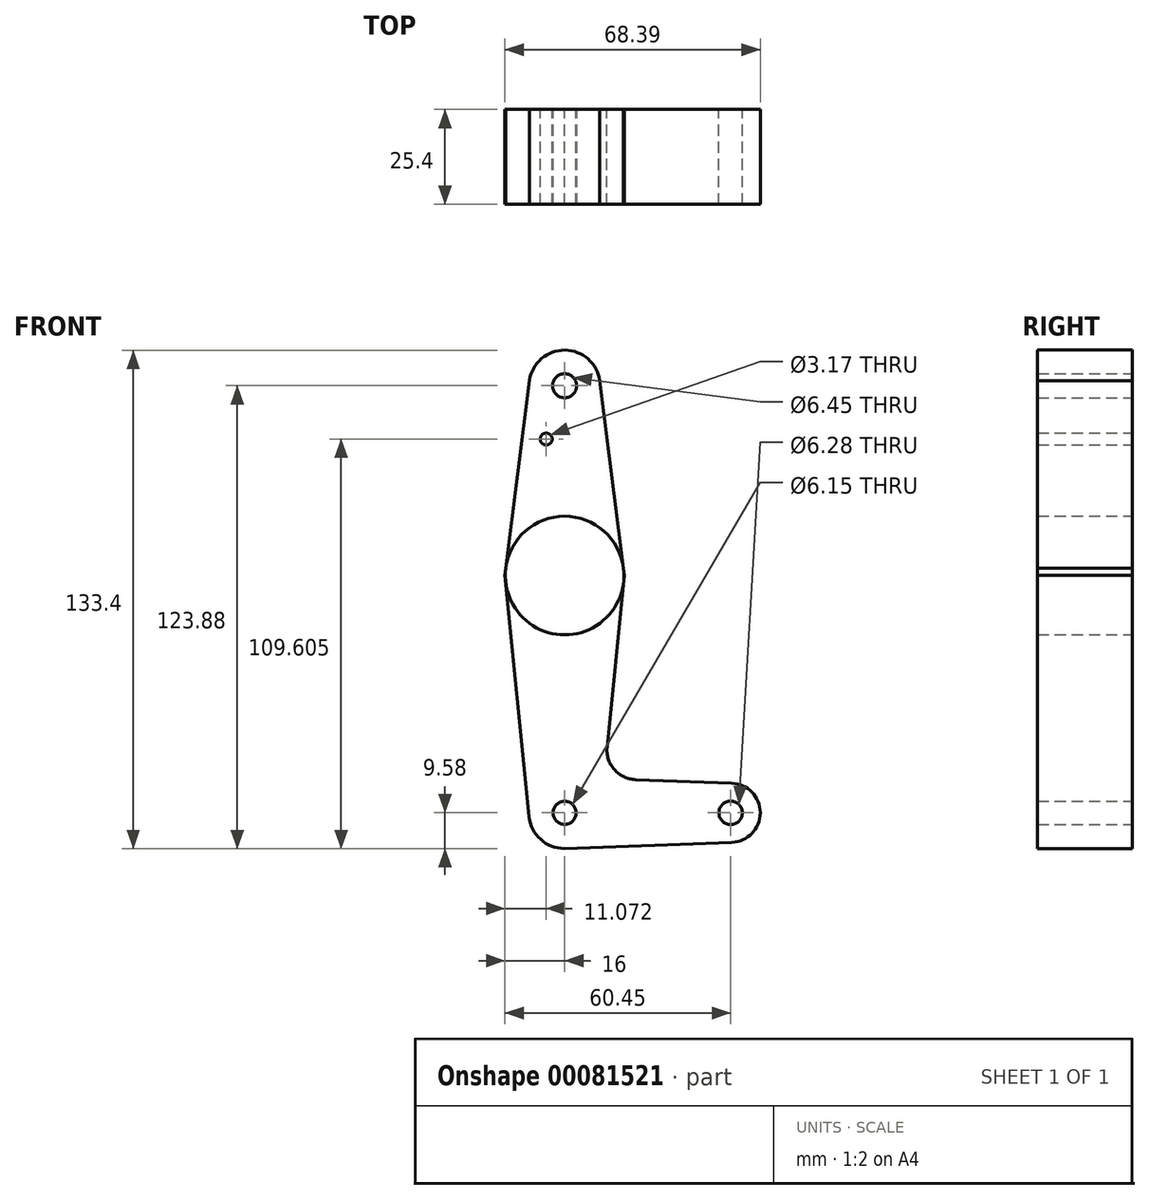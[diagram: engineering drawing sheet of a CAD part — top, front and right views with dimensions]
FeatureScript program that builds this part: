
annotation { "Feature Type Name" : "Feature", "Feature Type Description" : "" }
export const myFeature = defineFeature(function(context is Context, id is Id, definition is map)
    precondition{}
    {
        {
            var Q0;
            Q0=qCreatedBy(makeId("Front.planeOp"),FACE);
            var sketch = newSketch(context, id + "F0", { "sketchPlane" : qUnion([Q0])});
            skLineSegment(sketch, "E0", {"start": v(0, 50.8) * mm, "end": v(0, -63.5) * mm});
            skLineSegment(sketch, "E1", {"start": v(44.45, -63.5) * mm, "end": v(0, -63.5) * mm});
            skCircle(sketch, "E2", {"center": v(0, 50.8) * mm, "radius": 9.53 * mm});
            skCircle(sketch, "E3", {"center": v(0, 0) * mm, "radius": 15.88 * mm});
            skCircle(sketch, "E4", {"center": v(44.45, -63.5) * mm, "radius": 7.94 * mm});
            skCircle(sketch, "E5", {"center": v(0, -63.5) * mm, "radius": 9.58 * mm});
            skLineSegment(sketch, "E6", {"start": v(-9.42, 52.24) * mm, "end": v(-16, 0) * mm});
            skLineSegment(sketch, "E7", {"start": v(-16, 0) * mm, "end": v(-9.53, -64.46) * mm});
            skLineSegment(sketch, "E8", {"start": v(9.44, 52.09) * mm, "end": v(16, 0) * mm});
            skLineSegment(sketch, "E9", {"start": v(16, 0) * mm, "end": v(11.36, -45.88) * mm});
            skLineSegment(sketch, "E10", {"start": v(18.98, -54.62) * mm, "end": v(44.74, -55.57) * mm});
            skLineSegment(sketch, "E11", {"start": v(0, -73.08) * mm, "end": v(44.74, -71.43) * mm});
            skCircle(sketch, "E12", {"center": v(0, -63.5) * mm, "radius": 3.07 * mm});
            skCircle(sketch, "E13", {"center": v(44.45, -63.5) * mm, "radius": 3.14 * mm});
            skCircle(sketch, "E14", {"center": v(0, 0) * mm, "radius": 3.58 * mm});
            skCircle(sketch, "E15", {"center": v(0, 50.8) * mm, "radius": 3.23 * mm});
            skCircle(sketch, "E16", {"center": v(-4.93, 36.53) * mm, "radius": 1.59 * mm});
            skArc(sketch, "E17.filletArc", {"start": v(11.36, -45.88) * mm, "mid": v(13.27, -51.9) * mm, "end": v(18.98, -54.62) * mm});
            skSolve(sketch);
        }
        {
            var Q0;
            {var subQ0=sQuery(id+"F0.wireOp",EDGE,"E2");var subQ1=sQuery(id+"F0.wireOp",EDGE,"E0");var subQ2=makeQuery(id+"F0.imprint","INTERSECT",VERTEX,{"derivedFrom":[subQ1,subQ0]});Q0=makeQuery(id+"F0.imprint","IMPRINT",FACE,{"disambiguationData":[TD([[makeQuery(id+"F0.imprint","IMPRINT",EDGE,{"disambiguationData":[TD([[subQ2,-1.0]])],"derivedFrom":subQ1}),1.0]])]});}
            var Q1;
            Q1=makeQuery(id+"F0.imprint","IMPRINT",FACE,{"disambiguationData":[TD([[makeQuery(id+"F0.imprint","IMPRINT",EDGE,{"derivedFrom":sQuery(id+"F0.wireOp",EDGE,"E16")}),-1.0]])]});
            var Q2;
            {var subQ0=sQuery(id+"F0.wireOp",EDGE,"E3");var subQ2=sQuery(id+"F0.wireOp",EDGE,"E0");var subQ3=makeQuery(id+"F0.imprint","INTERSECT",VERTEX,{"disambiguationData":[OD(0.0)],"derivedFrom":[subQ2,subQ0]});Q2=makeQuery(id+"F0.imprint","IMPRINT",FACE,{"disambiguationData":[TD([[makeQuery(id+"F0.imprint","IMPRINT",EDGE,{"disambiguationData":[TD([[subQ3,-1.0]])],"derivedFrom":subQ2}),1.0]])]});}
            var Q3;
            {var subQ0=sQuery(id+"F0.wireOp",EDGE,"E3");var subQ2=sQuery(id+"F0.wireOp",EDGE,"E0");var subQ4=makeQuery(id+"F0.imprint","INTERSECT",VERTEX,{"disambiguationData":[OD(0.0)],"derivedFrom":[subQ2,subQ0]});Q3=makeQuery(id+"F0.imprint","IMPRINT",FACE,{"disambiguationData":[TD([[makeQuery(id+"F0.imprint","IMPRINT",EDGE,{"disambiguationData":[TD([[subQ4,-1.0]])],"derivedFrom":subQ2}),-1.0]])]});}
            var Q4;
            {var subQ0=sQuery(id+"F0.wireOp",EDGE,"E7");Q4=makeQuery(id+"F0.imprint","IMPRINT",FACE,{"disambiguationData":[TD([[makeQuery(id+"F0.imprint","IMPRINT",EDGE,{"derivedFrom":subQ0}),1.0]])]});}
            var Q5;
            {var subQ12=sQuery(id+"F0.wireOp",EDGE,"E9");Q5=makeQuery(id+"F0.imprint","IMPRINT",FACE,{"disambiguationData":[TD([[makeQuery(id+"F0.imprint","IMPRINT",EDGE,{"derivedFrom":subQ12}),-1.0]])]});}
            var Q6;
            {var subQ0=sQuery(id+"F0.wireOp",EDGE,"E4");var subQ1=sQuery(id+"F0.wireOp",EDGE,"E1");var subQ2=makeQuery(id+"F0.imprint","INTERSECT",VERTEX,{"derivedFrom":[subQ1,subQ0]});Q6=makeQuery(id+"F0.imprint","IMPRINT",FACE,{"disambiguationData":[TD([[makeQuery(id+"F0.imprint","IMPRINT",EDGE,{"disambiguationData":[TD([[subQ2,-1.0]])],"derivedFrom":subQ1}),1.0]])]});}
            var Q7;
            Q7=makeQuery(id+"F0.imprint","IMPRINT",FACE,{"disambiguationData":[TD([[makeQuery(id+"F0.imprint","IMPRINT",EDGE,{"derivedFrom":sQuery(id+"F0.wireOp",EDGE,"E15")}),-1.0]])]});
            var Q8;
            {var subQ0=sQuery(id+"F0.wireOp",EDGE,"E5");var subQ2=sQuery(id+"F0.wireOp",EDGE,"E0");var subQ3=makeQuery(id+"F0.imprint","INTERSECT",VERTEX,{"derivedFrom":[subQ2,subQ0]});Q8=makeQuery(id+"F0.imprint","IMPRINT",FACE,{"disambiguationData":[TD([[makeQuery(id+"F0.imprint","IMPRINT",EDGE,{"disambiguationData":[TD([[subQ3,-1.0]])],"derivedFrom":subQ2}),-1.0]])]});}
            var Q9;
            {var subQ0=sQuery(id+"F0.wireOp",EDGE,"E5");var subQ1=sQuery(id+"F0.wireOp",EDGE,"E0");var subQ2=makeQuery(id+"F0.imprint","INTERSECT",VERTEX,{"derivedFrom":[subQ1,subQ0]});Q9=makeQuery(id+"F0.imprint","IMPRINT",FACE,{"disambiguationData":[TD([[makeQuery(id+"F0.imprint","IMPRINT",EDGE,{"disambiguationData":[TD([[subQ2,-1.0]])],"derivedFrom":subQ1}),1.0]])]});}
            var Q10;
            Q10=makeQuery(id+"F0.imprint","IMPRINT",FACE,{"disambiguationData":[TD([[makeQuery(id+"F0.imprint","IMPRINT",EDGE,{"derivedFrom":sQuery(id+"F0.wireOp",EDGE,"E13")}),-1.0]])]});
            extrude(context, id + "F1", {"entities" : qUnion([Q0, Q1, Q2, Q3, Q4, Q5, Q6, Q7, Q8, Q9, Q10]), "depth" : 25.4 * mm});
        }
    });
